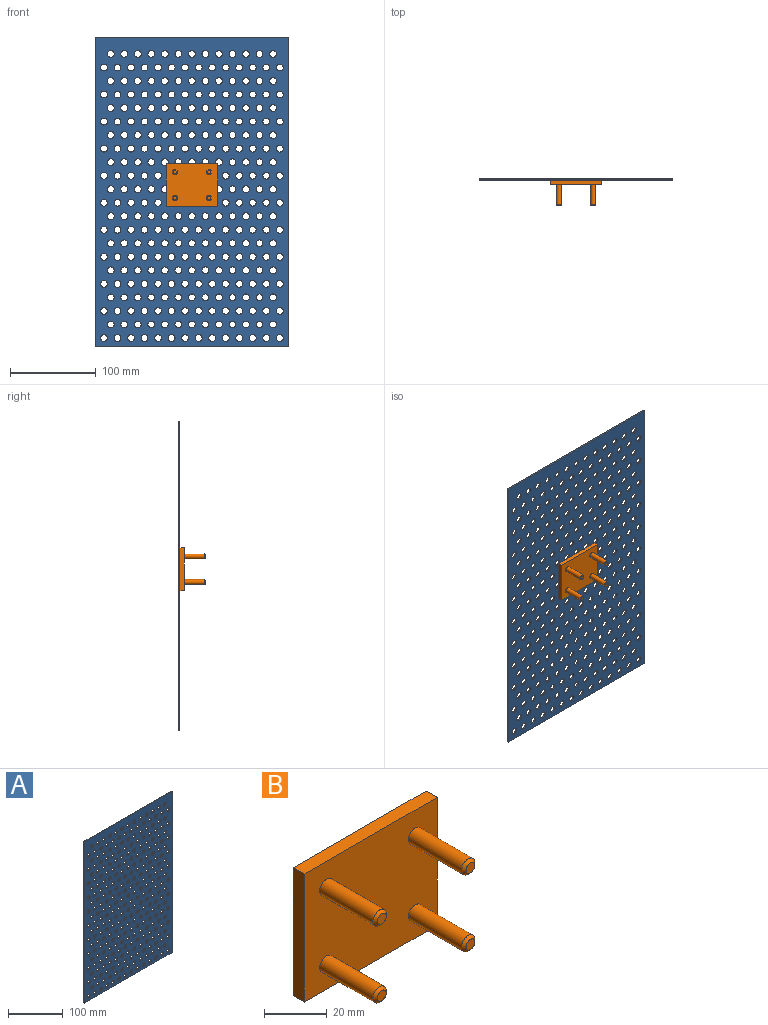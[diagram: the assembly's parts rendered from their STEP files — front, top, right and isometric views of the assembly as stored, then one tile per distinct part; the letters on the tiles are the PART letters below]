
ASSEMBLY  parts=2 mates=1
PART A: 303 faces, bbox 225x2x360 mm
  f0: plane 225x2mm, normal (0,0,1), area 450mm2, adj f1,f300,f301,f302
  f1: plane 360x2mm, normal (-1,0,0), area 720mm2, adj f0,f2,f301,f302
  f2: plane 225x2mm, normal (0,0,-1), area 450mm2, adj f1,f300,f301,f302
  f3: cylinder r=4mm len=8mm, axis (0,1,0), area 50.3mm2, adj f301,f302
  f4: cylinder r=4mm len=8mm, axis (0,1,0), area 50.3mm2, adj f301,f302
  f5: cylinder r=4mm len=8mm, axis (0,1,0), area 50.3mm2, adj f301,f302
  f6: cylinder r=4mm len=8mm, axis (0,1,0), area 50.3mm2, adj f301,f302
  f7: cylinder r=4mm len=8mm, axis (0,1,0), area 50.3mm2, adj f301,f302
  f8: cylinder r=4mm len=8mm, axis (0,1,0), area 50.3mm2, adj f301,f302
  f9: cylinder r=4mm len=8mm, axis (0,1,0), area 50.3mm2, adj f301,f302
  f10: cylinder r=4mm len=8mm, axis (0,1,0), area 50.3mm2, adj f301,f302
  f11: cylinder r=4mm len=8mm, axis (0,1,0), area 50.3mm2, adj f301,f302
  f12: cylinder r=4mm len=8mm, axis (0,1,0), area 50.3mm2, adj f301,f302
  f13: cylinder r=4mm len=8mm, axis (0,1,0), area 50.3mm2, adj f301,f302
  f14: cylinder r=4mm len=8mm, axis (0,1,0), area 50.3mm2, adj f301,f302
  f15: cylinder r=4mm len=8mm, axis (0,1,0), area 50.3mm2, adj f301,f302
  f16: cylinder r=4mm len=8mm, axis (0,1,0), area 50.3mm2, adj f301,f302
  f17: cylinder r=4mm len=8mm, axis (0,1,0), area 50.3mm2, adj f301,f302
  f18: cylinder r=4mm len=8mm, axis (0,1,0), area 50.3mm2, adj f301,f302
  f19: cylinder r=4mm len=8mm, axis (0,1,0), area 50.3mm2, adj f301,f302
  f20: cylinder r=4mm len=8mm, axis (0,1,0), area 50.3mm2, adj f301,f302
  f21: cylinder r=4mm len=8mm, axis (0,1,0), area 50.3mm2, adj f301,f302
  f22: cylinder r=4mm len=8mm, axis (0,1,0), area 50.3mm2, adj f301,f302
  f23: cylinder r=4mm len=8mm, axis (0,1,0), area 50.3mm2, adj f301,f302
  f24: cylinder r=4mm len=8mm, axis (0,1,0), area 50.3mm2, adj f301,f302
  f25: cylinder r=4mm len=8mm, axis (0,1,0), area 50.3mm2, adj f301,f302
  f26: cylinder r=4mm len=8mm, axis (0,1,0), area 50.3mm2, adj f301,f302
  f27: cylinder r=4mm len=8mm, axis (0,1,0), area 50.3mm2, adj f301,f302
  f28: cylinder r=4mm len=8mm, axis (0,1,0), area 50.3mm2, adj f301,f302
  f29: cylinder r=4mm len=8mm, axis (0,1,0), area 50.3mm2, adj f301,f302
  f30: cylinder r=4mm len=8mm, axis (0,1,0), area 50.3mm2, adj f301,f302
  f31: cylinder r=4mm len=8mm, axis (0,1,0), area 50.3mm2, adj f301,f302
  f32: cylinder r=4mm len=8mm, axis (0,1,0), area 50.3mm2, adj f301,f302
  f33: cylinder r=4mm len=8mm, axis (0,1,0), area 50.3mm2, adj f301,f302
  f34: cylinder r=4mm len=8mm, axis (0,1,0), area 50.3mm2, adj f301,f302
  f35: cylinder r=4mm len=8mm, axis (0,1,0), area 50.3mm2, adj f301,f302
  f36: cylinder r=4mm len=8mm, axis (0,1,0), area 50.3mm2, adj f301,f302
  f37: cylinder r=4mm len=8mm, axis (0,1,0), area 50.3mm2, adj f301,f302
  f38: cylinder r=4mm len=8mm, axis (0,1,0), area 50.3mm2, adj f301,f302
  f39: cylinder r=4mm len=8mm, axis (0,1,0), area 50.3mm2, adj f301,f302
  f40: cylinder r=4mm len=8mm, axis (0,1,0), area 50.3mm2, adj f301,f302
  f41: cylinder r=4mm len=8mm, axis (0,1,0), area 50.3mm2, adj f301,f302
  f42: cylinder r=4mm len=8mm, axis (0,1,0), area 50.3mm2, adj f301,f302
  f43: cylinder r=4mm len=8mm, axis (0,1,0), area 50.3mm2, adj f301,f302
  f44: cylinder r=4mm len=8mm, axis (0,1,0), area 50.3mm2, adj f301,f302
  f45: cylinder r=4mm len=8mm, axis (0,1,0), area 50.3mm2, adj f301,f302
  f46: cylinder r=4mm len=8mm, axis (0,1,0), area 50.3mm2, adj f301,f302
  f47: cylinder r=4mm len=8mm, axis (0,1,0), area 50.3mm2, adj f301,f302
  f48: cylinder r=4mm len=8mm, axis (0,1,0), area 50.3mm2, adj f301,f302
  f49: cylinder r=4mm len=8mm, axis (0,1,0), area 50.3mm2, adj f301,f302
  f50: cylinder r=4mm len=8mm, axis (0,1,0), area 50.3mm2, adj f301,f302
  f51: cylinder r=4mm len=8mm, axis (0,1,0), area 50.3mm2, adj f301,f302
  f52: cylinder r=4mm len=8mm, axis (0,1,0), area 50.3mm2, adj f301,f302
  f53: cylinder r=4mm len=8mm, axis (0,1,0), area 50.3mm2, adj f301,f302
  f54: cylinder r=4mm len=8mm, axis (0,1,0), area 50.3mm2, adj f301,f302
  f55: cylinder r=4mm len=8mm, axis (0,1,0), area 50.3mm2, adj f301,f302
  f56: cylinder r=4mm len=8mm, axis (0,1,0), area 50.3mm2, adj f301,f302
  f57: cylinder r=4mm len=8mm, axis (0,1,0), area 50.3mm2, adj f301,f302
  f58: cylinder r=4mm len=8mm, axis (0,1,0), area 50.3mm2, adj f301,f302
  f59: cylinder r=4mm len=8mm, axis (0,1,0), area 50.3mm2, adj f301,f302
  f60: cylinder r=4mm len=8mm, axis (0,1,0), area 50.3mm2, adj f301,f302
  f61: cylinder r=4mm len=8mm, axis (0,1,0), area 50.3mm2, adj f301,f302
  f62: cylinder r=4mm len=8mm, axis (0,1,0), area 50.3mm2, adj f301,f302
  f63: cylinder r=4mm len=8mm, axis (0,1,0), area 50.3mm2, adj f301,f302
  f64: cylinder r=4mm len=8mm, axis (0,1,0), area 50.3mm2, adj f301,f302
  f65: cylinder r=4mm len=8mm, axis (0,1,0), area 50.3mm2, adj f301,f302
  f66: cylinder r=4mm len=8mm, axis (0,1,0), area 50.3mm2, adj f301,f302
  f67: cylinder r=4mm len=8mm, axis (0,1,0), area 50.3mm2, adj f301,f302
  f68: cylinder r=4mm len=8mm, axis (0,1,0), area 50.3mm2, adj f301,f302
  f69: cylinder r=4mm len=8mm, axis (0,1,0), area 50.3mm2, adj f301,f302
  f70: cylinder r=4mm len=8mm, axis (0,1,0), area 50.3mm2, adj f301,f302
  f71: cylinder r=4mm len=8mm, axis (0,1,0), area 50.3mm2, adj f301,f302
  f72: cylinder r=4mm len=8mm, axis (0,1,0), area 50.3mm2, adj f301,f302
  f73: cylinder r=4mm len=8mm, axis (0,1,0), area 50.3mm2, adj f301,f302
  f74: cylinder r=4mm len=8mm, axis (0,1,0), area 50.3mm2, adj f301,f302
  f75: cylinder r=4mm len=8mm, axis (0,1,0), area 50.3mm2, adj f301,f302
  f76: cylinder r=4mm len=8mm, axis (0,1,0), area 50.3mm2, adj f301,f302
  f77: cylinder r=4mm len=8mm, axis (0,1,0), area 50.3mm2, adj f301,f302
  f78: cylinder r=4mm len=8mm, axis (0,1,0), area 50.3mm2, adj f301,f302
  f79: cylinder r=4mm len=8mm, axis (0,1,0), area 50.3mm2, adj f301,f302
  f80: cylinder r=4mm len=8mm, axis (0,1,0), area 50.3mm2, adj f301,f302
  f81: cylinder r=4mm len=8mm, axis (0,1,0), area 50.3mm2, adj f301,f302
  f82: cylinder r=4mm len=8mm, axis (0,1,0), area 50.3mm2, adj f301,f302
  f83: cylinder r=4mm len=8mm, axis (0,1,0), area 50.3mm2, adj f301,f302
  f84: cylinder r=4mm len=8mm, axis (0,1,0), area 50.3mm2, adj f301,f302
  f85: cylinder r=4mm len=8mm, axis (0,1,0), area 50.3mm2, adj f301,f302
  f86: cylinder r=4mm len=8mm, axis (0,1,0), area 50.3mm2, adj f301,f302
  f87: cylinder r=4mm len=8mm, axis (0,1,0), area 50.3mm2, adj f301,f302
  f88: cylinder r=4mm len=8mm, axis (0,1,0), area 50.3mm2, adj f301,f302
  f89: cylinder r=4mm len=8mm, axis (0,1,0), area 50.3mm2, adj f301,f302
  f90: cylinder r=4mm len=8mm, axis (0,1,0), area 50.3mm2, adj f301,f302
  f91: cylinder r=4mm len=8mm, axis (0,1,0), area 50.3mm2, adj f301,f302
  f92: cylinder r=4mm len=8mm, axis (0,1,0), area 50.3mm2, adj f301,f302
  f93: cylinder r=4mm len=8mm, axis (0,1,0), area 50.3mm2, adj f301,f302
  f94: cylinder r=4mm len=8mm, axis (0,1,0), area 50.3mm2, adj f301,f302
  f95: cylinder r=4mm len=8mm, axis (0,1,0), area 50.3mm2, adj f301,f302
  f96: cylinder r=4mm len=8mm, axis (0,1,0), area 50.3mm2, adj f301,f302
  f97: cylinder r=4mm len=8mm, axis (0,1,0), area 50.3mm2, adj f301,f302
  f98: cylinder r=4mm len=8mm, axis (0,1,0), area 50.3mm2, adj f301,f302
  f99: cylinder r=4mm len=8mm, axis (0,1,0), area 50.3mm2, adj f301,f302
  f100: cylinder r=4mm len=8mm, axis (0,1,0), area 50.3mm2, adj f301,f302
  f101: cylinder r=4mm len=8mm, axis (0,1,0), area 50.3mm2, adj f301,f302
  f102: cylinder r=4mm len=8mm, axis (0,1,0), area 50.3mm2, adj f301,f302
  f103: cylinder r=4mm len=8mm, axis (0,1,0), area 50.3mm2, adj f301,f302
  f104: cylinder r=4mm len=8mm, axis (0,1,0), area 50.3mm2, adj f301,f302
  f105: cylinder r=4mm len=8mm, axis (0,1,0), area 50.3mm2, adj f301,f302
  f106: cylinder r=4mm len=8mm, axis (0,1,0), area 50.3mm2, adj f301,f302
  f107: cylinder r=4mm len=8mm, axis (0,1,0), area 50.3mm2, adj f301,f302
  f108: cylinder r=4mm len=8mm, axis (0,1,0), area 50.3mm2, adj f301,f302
  f109: cylinder r=4mm len=8mm, axis (0,1,0), area 50.3mm2, adj f301,f302
  f110: cylinder r=4mm len=8mm, axis (0,1,0), area 50.3mm2, adj f301,f302
  f111: cylinder r=4mm len=8mm, axis (0,1,0), area 50.3mm2, adj f301,f302
  f112: cylinder r=4mm len=8mm, axis (0,1,0), area 50.3mm2, adj f301,f302
  f113: cylinder r=4mm len=8mm, axis (0,1,0), area 50.3mm2, adj f301,f302
  f114: cylinder r=4mm len=8mm, axis (0,1,0), area 50.3mm2, adj f301,f302
  f115: cylinder r=4mm len=8mm, axis (0,1,0), area 50.3mm2, adj f301,f302
  f116: cylinder r=4mm len=8mm, axis (0,1,0), area 50.3mm2, adj f301,f302
  f117: cylinder r=4mm len=8mm, axis (0,1,0), area 50.3mm2, adj f301,f302
  f118: cylinder r=4mm len=8mm, axis (0,1,0), area 50.3mm2, adj f301,f302
  f119: cylinder r=4mm len=8mm, axis (0,1,0), area 50.3mm2, adj f301,f302
  f120: cylinder r=4mm len=8mm, axis (0,1,0), area 50.3mm2, adj f301,f302
  f121: cylinder r=4mm len=8mm, axis (0,1,0), area 50.3mm2, adj f301,f302
  f122: cylinder r=4mm len=8mm, axis (0,1,0), area 50.3mm2, adj f301,f302
  f123: cylinder r=4mm len=8mm, axis (0,1,0), area 50.3mm2, adj f301,f302
  f124: cylinder r=4mm len=8mm, axis (0,1,0), area 50.3mm2, adj f301,f302
  f125: cylinder r=4mm len=8mm, axis (0,1,0), area 50.3mm2, adj f301,f302
  f126: cylinder r=4mm len=8mm, axis (0,1,0), area 50.3mm2, adj f301,f302
  f127: cylinder r=4mm len=8mm, axis (0,1,0), area 50.3mm2, adj f301,f302
  f128: cylinder r=4mm len=8mm, axis (0,1,0), area 50.3mm2, adj f301,f302
  f129: cylinder r=4mm len=8mm, axis (0,1,0), area 50.3mm2, adj f301,f302
  f130: cylinder r=4mm len=8mm, axis (0,1,0), area 50.3mm2, adj f301,f302
  f131: cylinder r=4mm len=8mm, axis (0,1,0), area 50.3mm2, adj f301,f302
  f132: cylinder r=4mm len=8mm, axis (0,1,0), area 50.3mm2, adj f301,f302
  f133: cylinder r=4mm len=8mm, axis (0,1,0), area 50.3mm2, adj f301,f302
  f134: cylinder r=4mm len=8mm, axis (0,1,0), area 50.3mm2, adj f301,f302
  f135: cylinder r=4mm len=8mm, axis (0,1,0), area 50.3mm2, adj f301,f302
  f136: cylinder r=4mm len=8mm, axis (0,1,0), area 50.3mm2, adj f301,f302
  f137: cylinder r=4mm len=8mm, axis (0,1,0), area 50.3mm2, adj f301,f302
  f138: cylinder r=4mm len=8mm, axis (0,1,0), area 50.3mm2, adj f301,f302
  f139: cylinder r=4mm len=8mm, axis (0,1,0), area 50.3mm2, adj f301,f302
  f140: cylinder r=4mm len=8mm, axis (0,1,0), area 50.3mm2, adj f301,f302
  f141: cylinder r=4mm len=8mm, axis (0,1,0), area 50.3mm2, adj f301,f302
  f142: cylinder r=4mm len=8mm, axis (0,1,0), area 50.3mm2, adj f301,f302
  f143: cylinder r=4mm len=8mm, axis (0,1,0), area 50.3mm2, adj f301,f302
  f144: cylinder r=4mm len=8mm, axis (0,1,0), area 50.3mm2, adj f301,f302
  f145: cylinder r=4mm len=8mm, axis (0,1,0), area 50.3mm2, adj f301,f302
  f146: cylinder r=4mm len=8mm, axis (0,1,0), area 50.3mm2, adj f301,f302
  f147: cylinder r=4mm len=8mm, axis (0,1,0), area 50.3mm2, adj f301,f302
  f148: cylinder r=4mm len=8mm, axis (0,1,0), area 50.3mm2, adj f301,f302
  f149: cylinder r=4mm len=8mm, axis (0,1,0), area 50.3mm2, adj f301,f302
  f150: cylinder r=4mm len=8mm, axis (0,1,0), area 50.3mm2, adj f301,f302
  f151: cylinder r=4mm len=8mm, axis (0,1,0), area 50.3mm2, adj f301,f302
  f152: cylinder r=4mm len=8mm, axis (0,1,0), area 50.3mm2, adj f301,f302
  f153: cylinder r=4mm len=8mm, axis (0,1,0), area 50.3mm2, adj f301,f302
  f154: cylinder r=4mm len=8mm, axis (0,1,0), area 50.3mm2, adj f301,f302
  f155: cylinder r=4mm len=8mm, axis (0,1,0), area 50.3mm2, adj f301,f302
  f156: cylinder r=4mm len=8mm, axis (0,1,0), area 50.3mm2, adj f301,f302
  f157: cylinder r=4mm len=8mm, axis (0,1,0), area 50.3mm2, adj f301,f302
  f158: cylinder r=4mm len=8mm, axis (0,1,0), area 50.3mm2, adj f301,f302
  f159: cylinder r=4mm len=8mm, axis (0,1,0), area 50.3mm2, adj f301,f302
  f160: cylinder r=4mm len=8mm, axis (0,1,0), area 50.3mm2, adj f301,f302
  f161: cylinder r=4mm len=8mm, axis (0,1,0), area 50.3mm2, adj f301,f302
  f162: cylinder r=4mm len=8mm, axis (0,1,0), area 50.3mm2, adj f301,f302
  f163: cylinder r=4mm len=8mm, axis (0,1,0), area 50.3mm2, adj f301,f302
  f164: cylinder r=4mm len=8mm, axis (0,1,0), area 50.3mm2, adj f301,f302
  f165: cylinder r=4mm len=8mm, axis (0,1,0), area 50.3mm2, adj f301,f302
  f166: cylinder r=4mm len=8mm, axis (0,1,0), area 50.3mm2, adj f301,f302
  f167: cylinder r=4mm len=8mm, axis (0,1,0), area 50.3mm2, adj f301,f302
  f168: cylinder r=4mm len=8mm, axis (0,1,0), area 50.3mm2, adj f301,f302
  f169: cylinder r=4mm len=8mm, axis (0,1,0), area 50.3mm2, adj f301,f302
  f170: cylinder r=4mm len=8mm, axis (0,1,0), area 50.3mm2, adj f301,f302
  f171: cylinder r=4mm len=8mm, axis (0,1,0), area 50.3mm2, adj f301,f302
  f172: cylinder r=4mm len=8mm, axis (0,1,0), area 50.3mm2, adj f301,f302
  f173: cylinder r=4mm len=8mm, axis (0,1,0), area 50.3mm2, adj f301,f302
  f174: cylinder r=4mm len=8mm, axis (0,1,0), area 50.3mm2, adj f301,f302
  f175: cylinder r=4mm len=8mm, axis (0,1,0), area 50.3mm2, adj f301,f302
  f176: cylinder r=4mm len=8mm, axis (0,1,0), area 50.3mm2, adj f301,f302
  f177: cylinder r=4mm len=8mm, axis (0,1,0), area 50.3mm2, adj f301,f302
  f178: cylinder r=4mm len=8mm, axis (0,1,0), area 50.3mm2, adj f301,f302
  f179: cylinder r=4mm len=8mm, axis (0,1,0), area 50.3mm2, adj f301,f302
  f180: cylinder r=4mm len=8mm, axis (0,1,0), area 50.3mm2, adj f301,f302
  f181: cylinder r=4mm len=8mm, axis (0,1,0), area 50.3mm2, adj f301,f302
  f182: cylinder r=4mm len=8mm, axis (0,1,0), area 50.3mm2, adj f301,f302
  f183: cylinder r=4mm len=8mm, axis (0,1,0), area 50.3mm2, adj f301,f302
  f184: cylinder r=4mm len=8mm, axis (0,1,0), area 50.3mm2, adj f301,f302
  f185: cylinder r=4mm len=8mm, axis (0,1,0), area 50.3mm2, adj f301,f302
  f186: cylinder r=4mm len=8mm, axis (0,1,0), area 50.3mm2, adj f301,f302
  f187: cylinder r=4mm len=8mm, axis (0,1,0), area 50.3mm2, adj f301,f302
  f188: cylinder r=4mm len=8mm, axis (0,1,0), area 50.3mm2, adj f301,f302
  f189: cylinder r=4mm len=8mm, axis (0,1,0), area 50.3mm2, adj f301,f302
  f190: cylinder r=4mm len=8mm, axis (0,1,0), area 50.3mm2, adj f301,f302
  f191: cylinder r=4mm len=8mm, axis (0,1,0), area 50.3mm2, adj f301,f302
  f192: cylinder r=4mm len=8mm, axis (0,1,0), area 50.3mm2, adj f301,f302
  f193: cylinder r=4mm len=8mm, axis (0,1,0), area 50.3mm2, adj f301,f302
  f194: cylinder r=4mm len=8mm, axis (0,1,0), area 50.3mm2, adj f301,f302
  f195: cylinder r=4mm len=8mm, axis (0,1,0), area 50.3mm2, adj f301,f302
  f196: cylinder r=4mm len=8mm, axis (0,1,0), area 50.3mm2, adj f301,f302
  f197: cylinder r=4mm len=8mm, axis (0,1,0), area 50.3mm2, adj f301,f302
  f198: cylinder r=4mm len=8mm, axis (0,1,0), area 50.3mm2, adj f301,f302
  f199: cylinder r=4mm len=8mm, axis (0,1,0), area 50.3mm2, adj f301,f302
  f200: cylinder r=4mm len=8mm, axis (0,1,0), area 50.3mm2, adj f301,f302
  f201: cylinder r=4mm len=8mm, axis (0,1,0), area 50.3mm2, adj f301,f302
  f202: cylinder r=4mm len=8mm, axis (0,1,0), area 50.3mm2, adj f301,f302
  f203: cylinder r=4mm len=8mm, axis (0,1,0), area 50.3mm2, adj f301,f302
  f204: cylinder r=4mm len=8mm, axis (0,1,0), area 50.3mm2, adj f301,f302
  f205: cylinder r=4mm len=8mm, axis (0,1,0), area 50.3mm2, adj f301,f302
  f206: cylinder r=4mm len=8mm, axis (0,1,0), area 50.3mm2, adj f301,f302
  f207: cylinder r=4mm len=8mm, axis (0,1,0), area 50.3mm2, adj f301,f302
  f208: cylinder r=4mm len=8mm, axis (0,1,0), area 50.3mm2, adj f301,f302
  f209: cylinder r=4mm len=8mm, axis (0,1,0), area 50.3mm2, adj f301,f302
  f210: cylinder r=4mm len=8mm, axis (0,1,0), area 50.3mm2, adj f301,f302
  f211: cylinder r=4mm len=8mm, axis (0,1,0), area 50.3mm2, adj f301,f302
  f212: cylinder r=4mm len=8mm, axis (0,1,0), area 50.3mm2, adj f301,f302
  f213: cylinder r=4mm len=8mm, axis (0,1,0), area 50.3mm2, adj f301,f302
  f214: cylinder r=4mm len=8mm, axis (0,1,0), area 50.3mm2, adj f301,f302
  f215: cylinder r=4mm len=8mm, axis (0,1,0), area 50.3mm2, adj f301,f302
  f216: cylinder r=4mm len=8mm, axis (0,1,0), area 50.3mm2, adj f301,f302
  f217: cylinder r=4mm len=8mm, axis (0,1,0), area 50.3mm2, adj f301,f302
  f218: cylinder r=4mm len=8mm, axis (0,1,0), area 50.3mm2, adj f301,f302
  f219: cylinder r=4mm len=8mm, axis (0,1,0), area 50.3mm2, adj f301,f302
  f220: cylinder r=4mm len=8mm, axis (0,1,0), area 50.3mm2, adj f301,f302
  f221: cylinder r=4mm len=8mm, axis (0,1,0), area 50.3mm2, adj f301,f302
  f222: cylinder r=4mm len=8mm, axis (0,1,0), area 50.3mm2, adj f301,f302
  f223: cylinder r=4mm len=8mm, axis (0,1,0), area 50.3mm2, adj f301,f302
  f224: cylinder r=4mm len=8mm, axis (0,1,0), area 50.3mm2, adj f301,f302
  f225: cylinder r=4mm len=8mm, axis (0,1,0), area 50.3mm2, adj f301,f302
  f226: cylinder r=4mm len=8mm, axis (0,1,0), area 50.3mm2, adj f301,f302
  f227: cylinder r=4mm len=8mm, axis (0,1,0), area 50.3mm2, adj f301,f302
  f228: cylinder r=4mm len=8mm, axis (0,1,0), area 50.3mm2, adj f301,f302
  f229: cylinder r=4mm len=8mm, axis (0,1,0), area 50.3mm2, adj f301,f302
  f230: cylinder r=4mm len=8mm, axis (0,1,0), area 50.3mm2, adj f301,f302
  f231: cylinder r=4mm len=8mm, axis (0,1,0), area 50.3mm2, adj f301,f302
  f232: cylinder r=4mm len=8mm, axis (0,1,0), area 50.3mm2, adj f301,f302
  f233: cylinder r=4mm len=8mm, axis (0,1,0), area 50.3mm2, adj f301,f302
  f234: cylinder r=4mm len=8mm, axis (0,1,0), area 50.3mm2, adj f301,f302
  f235: cylinder r=4mm len=8mm, axis (0,1,0), area 50.3mm2, adj f301,f302
  f236: cylinder r=4mm len=8mm, axis (0,1,0), area 50.3mm2, adj f301,f302
  f237: cylinder r=4mm len=8mm, axis (0,1,0), area 50.3mm2, adj f301,f302
  f238: cylinder r=4mm len=8mm, axis (0,1,0), area 50.3mm2, adj f301,f302
  f239: cylinder r=4mm len=8mm, axis (0,1,0), area 50.3mm2, adj f301,f302
  f240: cylinder r=4mm len=8mm, axis (0,1,0), area 50.3mm2, adj f301,f302
  f241: cylinder r=4mm len=8mm, axis (0,1,0), area 50.3mm2, adj f301,f302
  f242: cylinder r=4mm len=8mm, axis (0,1,0), area 50.3mm2, adj f301,f302
  f243: cylinder r=4mm len=8mm, axis (0,1,0), area 50.3mm2, adj f301,f302
  f244: cylinder r=4mm len=8mm, axis (0,1,0), area 50.3mm2, adj f301,f302
  f245: cylinder r=4mm len=8mm, axis (0,1,0), area 50.3mm2, adj f301,f302
  f246: cylinder r=4mm len=8mm, axis (0,1,0), area 50.3mm2, adj f301,f302
  f247: cylinder r=4mm len=8mm, axis (0,1,0), area 50.3mm2, adj f301,f302
  f248: cylinder r=4mm len=8mm, axis (0,1,0), area 50.3mm2, adj f301,f302
  f249: cylinder r=4mm len=8mm, axis (0,1,0), area 50.3mm2, adj f301,f302
  f250: cylinder r=4mm len=8mm, axis (0,1,0), area 50.3mm2, adj f301,f302
  f251: cylinder r=4mm len=8mm, axis (0,1,0), area 50.3mm2, adj f301,f302
  f252: cylinder r=4mm len=8mm, axis (0,1,0), area 50.3mm2, adj f301,f302
  f253: cylinder r=4mm len=8mm, axis (0,1,0), area 50.3mm2, adj f301,f302
  f254: cylinder r=4mm len=8mm, axis (0,1,0), area 50.3mm2, adj f301,f302
  f255: cylinder r=4mm len=8mm, axis (0,1,0), area 50.3mm2, adj f301,f302
  f256: cylinder r=4mm len=8mm, axis (0,1,0), area 50.3mm2, adj f301,f302
  f257: cylinder r=4mm len=8mm, axis (0,1,0), area 50.3mm2, adj f301,f302
  f258: cylinder r=4mm len=8mm, axis (0,1,0), area 50.3mm2, adj f301,f302
  f259: cylinder r=4mm len=8mm, axis (0,1,0), area 50.3mm2, adj f301,f302
  f260: cylinder r=4mm len=8mm, axis (0,1,0), area 50.3mm2, adj f301,f302
  f261: cylinder r=4mm len=8mm, axis (0,1,0), area 50.3mm2, adj f301,f302
  f262: cylinder r=4mm len=8mm, axis (0,1,0), area 50.3mm2, adj f301,f302
  f263: cylinder r=4mm len=8mm, axis (0,1,0), area 50.3mm2, adj f301,f302
  f264: cylinder r=4mm len=8mm, axis (0,1,0), area 50.3mm2, adj f301,f302
  f265: cylinder r=4mm len=8mm, axis (0,1,0), area 50.3mm2, adj f301,f302
  f266: cylinder r=4mm len=8mm, axis (0,1,0), area 50.3mm2, adj f301,f302
  f267: cylinder r=4mm len=8mm, axis (0,1,0), area 50.3mm2, adj f301,f302
  f268: cylinder r=4mm len=8mm, axis (0,1,0), area 50.3mm2, adj f301,f302
  f269: cylinder r=4mm len=8mm, axis (0,1,0), area 50.3mm2, adj f301,f302
  f270: cylinder r=4mm len=8mm, axis (0,1,0), area 50.3mm2, adj f301,f302
  f271: cylinder r=4mm len=8mm, axis (0,1,0), area 50.3mm2, adj f301,f302
  f272: cylinder r=4mm len=8mm, axis (0,1,0), area 50.3mm2, adj f301,f302
  f273: cylinder r=4mm len=8mm, axis (0,1,0), area 50.3mm2, adj f301,f302
  f274: cylinder r=4mm len=8mm, axis (0,1,0), area 50.3mm2, adj f301,f302
  f275: cylinder r=4mm len=8mm, axis (0,1,0), area 50.3mm2, adj f301,f302
  f276: cylinder r=4mm len=8mm, axis (0,1,0), area 50.3mm2, adj f301,f302
  f277: cylinder r=4mm len=8mm, axis (0,1,0), area 50.3mm2, adj f301,f302
  f278: cylinder r=4mm len=8mm, axis (0,1,0), area 50.3mm2, adj f301,f302
  f279: cylinder r=4mm len=8mm, axis (0,1,0), area 50.3mm2, adj f301,f302
  f280: cylinder r=4mm len=8mm, axis (0,1,0), area 50.3mm2, adj f301,f302
  f281: cylinder r=4mm len=8mm, axis (0,1,0), area 50.3mm2, adj f301,f302
  f282: cylinder r=4mm len=8mm, axis (0,1,0), area 50.3mm2, adj f301,f302
  f283: cylinder r=4mm len=8mm, axis (0,1,0), area 50.3mm2, adj f301,f302
  f284: cylinder r=4mm len=8mm, axis (0,1,0), area 50.3mm2, adj f301,f302
  f285: cylinder r=4mm len=8mm, axis (0,1,0), area 50.3mm2, adj f301,f302
  f286: cylinder r=4mm len=8mm, axis (0,1,0), area 50.3mm2, adj f301,f302
  f287: cylinder r=4mm len=8mm, axis (0,1,0), area 50.3mm2, adj f301,f302
  f288: cylinder r=4mm len=8mm, axis (0,1,0), area 50.3mm2, adj f301,f302
  f289: cylinder r=4mm len=8mm, axis (0,1,0), area 50.3mm2, adj f301,f302
  f290: cylinder r=4mm len=8mm, axis (0,1,0), area 50.3mm2, adj f301,f302
  f291: cylinder r=4mm len=8mm, axis (0,1,0), area 50.3mm2, adj f301,f302
  f292: cylinder r=4mm len=8mm, axis (0,1,0), area 50.3mm2, adj f301,f302
  f293: cylinder r=4mm len=8mm, axis (0,1,0), area 50.3mm2, adj f301,f302
  f294: cylinder r=4mm len=8mm, axis (0,1,0), area 50.3mm2, adj f301,f302
  f295: cylinder r=4mm len=8mm, axis (0,1,0), area 50.3mm2, adj f301,f302
  f296: cylinder r=4mm len=8mm, axis (0,1,0), area 50.3mm2, adj f301,f302
  f297: cylinder r=4mm len=8mm, axis (0,1,0), area 50.3mm2, adj f301,f302
  f298: cylinder r=4mm len=8mm, axis (0,1,0), area 50.3mm2, adj f301,f302
  f299: cylinder r=4mm len=8mm, axis (0,1,0), area 50.3mm2, adj f301,f302
  f300: plane 360x2mm, normal (1,0,0), area 720mm2, adj f0,f2,f301,f302
  f301: plane 360x225mm, normal (0,-1,0), area 66071.2mm2, adj f0,f1,f2,f3,f4,f5,f6,f7
  f302: plane 360x225mm, normal (0,1,0), area 66071.2mm2, adj f0,f1,f2,f3,f4,f5,f6,f7
PART B: 18 faces, bbox 60x30x50 mm
  f0: plane 60x5mm, normal (0,0,1), area 300mm2, adj f1,f3,f4,f5
  f1: plane 50x5mm, normal (-1,0,0), area 250mm2, adj f0,f2,f4,f5
  f2: plane 60x5mm, normal (0,0,-1), area 300mm2, adj f1,f3,f4,f5
  f3: plane 50x5mm, normal (1,0,0), area 250mm2, adj f0,f2,f4,f5
  f4: plane 60x50mm, normal (0,-1,0), area 2886.9mm2, adj f0,f1,f2,f3,f6,f8,f10,f12
  f5: plane 60x50mm, normal (0,1,0), area 3000mm2, adj f0,f1,f2,f3
  f6: cylinder r=3mm len=24mm, axis (0,1,0), area 452.4mm2, adj f4,f16
  f7: plane 4x4mm, normal (0,-1,0), area 12.6mm2, adj f16
  f8: cylinder r=3mm len=24mm, axis (0,1,0), area 452.4mm2, adj f4,f15
  f9: plane 4x4mm, normal (0,-1,0), area 12.6mm2, adj f15
  f10: cylinder r=3mm len=24mm, axis (0,1,0), area 452.4mm2, adj f4,f17
  f11: plane 4x4mm, normal (0,-1,0), area 12.6mm2, adj f17
  f12: cylinder r=3mm len=24mm, axis (0,1,0), area 452.4mm2, adj f4,f14
  f13: plane 4x4mm, normal (0,-1,0), area 12.6mm2, adj f14
  f14: cone r=2mm half-angle=45deg, axis (0,1,0), area 22.2mm2, adj f12,f13
  f15: cone r=3mm half-angle=45deg, axis (0,1,0), area 22.2mm2, adj f8,f9
  f16: cone r=2mm half-angle=45deg, axis (0,1,0), area 22.2mm2, adj f6,f7
  f17: cone r=3mm half-angle=45deg, axis (0,1,0), area 22.2mm2, adj f10,f11
PLACE A t=(-67.01,-71.81,10.69)mm
PLACE B t=(-67.01,-73.81,18.69)mm
MATE fastened B.f5 <-> A.f301  axis (0,1,0) through (-67.01,-73.81,-6.31)mm
